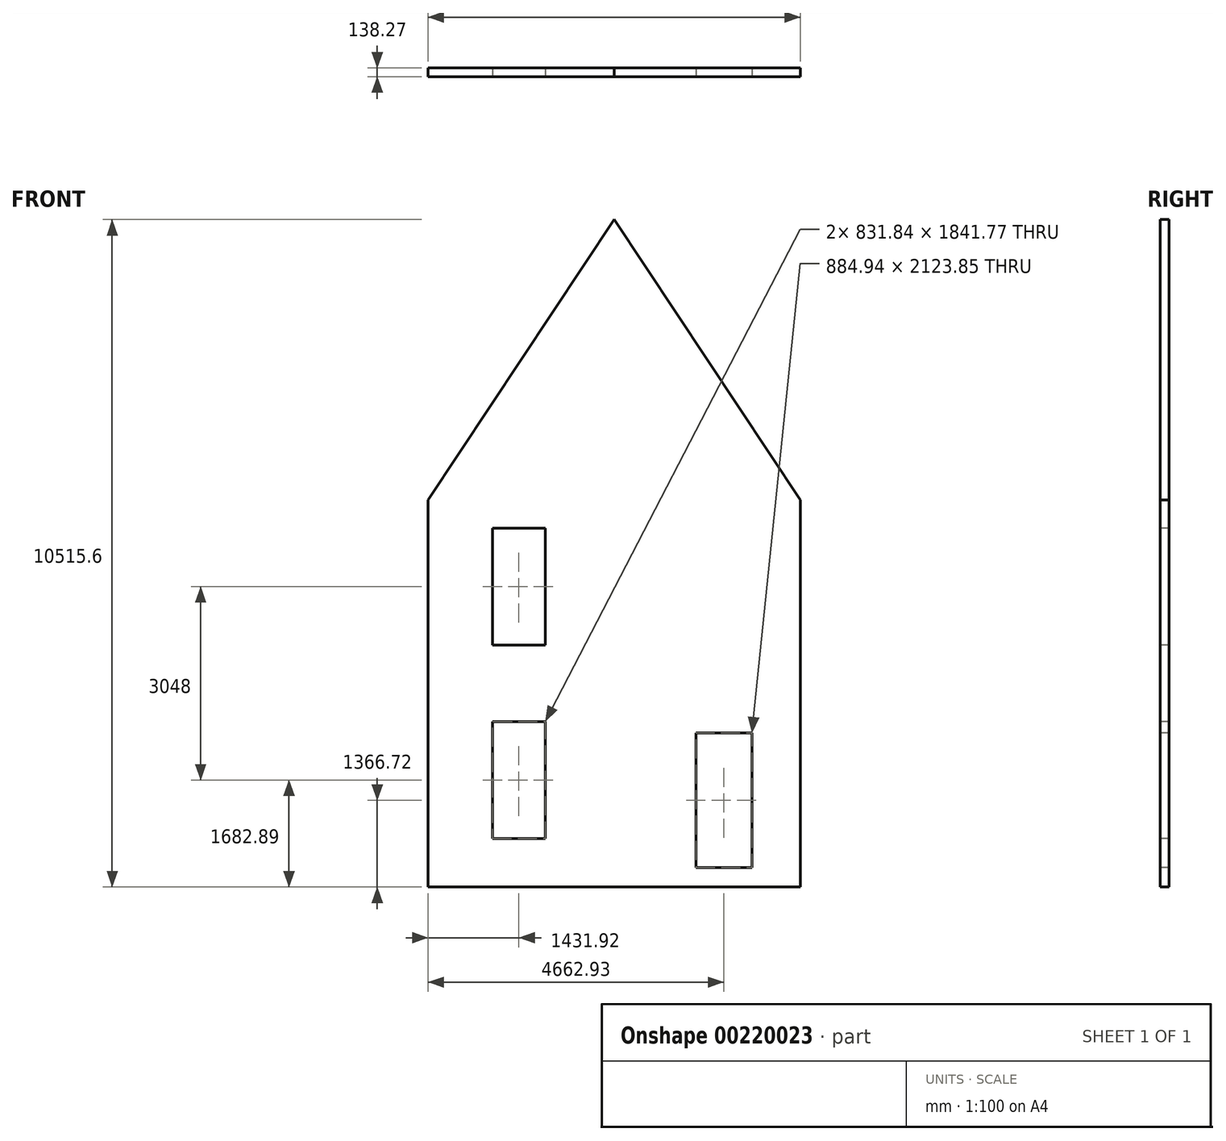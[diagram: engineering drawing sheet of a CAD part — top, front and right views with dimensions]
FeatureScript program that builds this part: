
annotation { "Feature Type Name" : "Feature", "Feature Type Description" : "" }
export const myFeature = defineFeature(function(context is Context, id is Id, definition is map)
    precondition{}
    {
        {
            var Q0;
            Q0=qCreatedBy(makeId("Front.planeOp"),FACE);
            var sketch = newSketch(context, id + "F0", { "sketchPlane" : qUnion([Q0])});
            skLineSegment(sketch, "E0", {"start": v(0, 0) * mm, "end": v(5867.4, 0) * mm});
            skLineSegment(sketch, "E1", {"start": v(5867.4, 0) * mm, "end": v(5867.4, 6096) * mm});
            skLineSegment(sketch, "E2", {"start": v(5867.4, 6096) * mm, "end": v(2933.7, 10515.6) * mm});
            skLineSegment(sketch, "E3", {"start": v(2933.7, 10515.6) * mm, "end": v(0, 6096) * mm});
            skLineSegment(sketch, "E4", {"start": v(0, 6096) * mm, "end": v(0, 0) * mm});
            skSolve(sketch);
        }
        {
            var Q0;
            Q0=makeQuery(id+"F0.imprint","IMPRINT",FACE,{"disambiguationData":[TD([[makeQuery(id+"F0.imprint","IMPRINT",EDGE,{"derivedFrom":sQuery(id+"F0.wireOp",EDGE,"E0")}),1.0]])]});
            extrude(context, id + "F1", {"entities" : qUnion([Q0]), "depth" : 138.27 * mm});
        }
        {
            var Q0;
            Q0=makeQuery(id+"F1.opExtrude","CAP_FACE",FACE,{"disambiguationData":[OSD([sQuery(id+"F0.wireOp",EDGE,"E0"),sQuery(id+"F0.wireOp",EDGE,"E1"),sQuery(id+"F0.wireOp",EDGE,"E2"),sQuery(id+"F0.wireOp",EDGE,"E3"),sQuery(id+"F0.wireOp",EDGE,"E4")])],"isStart":false});
            var sketch = newSketch(context, id + "F2", { "sketchPlane" : qUnion([Q0])});
            skLineSegment(sketch, "E5.bottom", {"start": v(4220.46, 2428.65) * mm, "end": v(5105.4, 2428.65) * mm});
            skLineSegment(sketch, "E5.top", {"start": v(4220.46, 304.8) * mm, "end": v(5105.4, 304.8) * mm});
            skLineSegment(sketch, "E5.left", {"start": v(4220.46, 2428.65) * mm, "end": v(4220.46, 304.8) * mm});
            skLineSegment(sketch, "E5.right", {"start": v(5105.4, 2428.65) * mm, "end": v(5105.4, 304.8) * mm});
            skLineSegment(sketch, "E6.bottom", {"start": v(1016, 2603.77) * mm, "end": v(1847.84, 2603.77) * mm});
            skLineSegment(sketch, "E6.top", {"start": v(1016, 762) * mm, "end": v(1847.84, 762) * mm});
            skLineSegment(sketch, "E6.left", {"start": v(1016, 2603.77) * mm, "end": v(1016, 762) * mm});
            skLineSegment(sketch, "E6.right", {"start": v(1847.84, 2603.77) * mm, "end": v(1847.84, 762) * mm});
            skLineSegment(sketch, "E7.bottom", {"start": v(1016, 3810) * mm, "end": v(1847.84, 3810) * mm});
            skLineSegment(sketch, "E7.top", {"start": v(1016, 5651.77) * mm, "end": v(1847.84, 5651.77) * mm});
            skLineSegment(sketch, "E7.left", {"start": v(1016, 3810) * mm, "end": v(1016, 5651.77) * mm});
            skLineSegment(sketch, "E7.right", {"start": v(1847.84, 3810) * mm, "end": v(1847.84, 5651.77) * mm});
            skSolve(sketch);
        }
        {
            var Q0;
            Q0=makeQuery(id+"F2.imprint","IMPRINT",FACE,{"disambiguationData":[TD([[makeQuery(id+"F2.imprint","IMPRINT",EDGE,{"derivedFrom":sQuery(id+"F2.wireOp",EDGE,"E6.bottom")}),-1.0]])]});
            var Q1;
            Q1=makeQuery(id+"F2.imprint","IMPRINT",FACE,{"disambiguationData":[TD([[makeQuery(id+"F2.imprint","IMPRINT",EDGE,{"derivedFrom":sQuery(id+"F2.wireOp",EDGE,"E5.bottom")}),-1.0]])]});
            var Q2;
            Q2=makeQuery(id+"F2.imprint","IMPRINT",FACE,{"disambiguationData":[TD([[makeQuery(id+"F2.imprint","IMPRINT",EDGE,{"derivedFrom":sQuery(id+"F2.wireOp",EDGE,"E7.bottom")}),1.0]])]});
            extrude(context, id + "F3", {"entities" : qUnion([Q0, Q1, Q2]), "operationType" : NewBodyOperationType.REMOVE, "endBound" : BoundingType.THROUGH_ALL, "oppositeDirection" : true, "depth" : 25.4 * mm});
        }
    });
